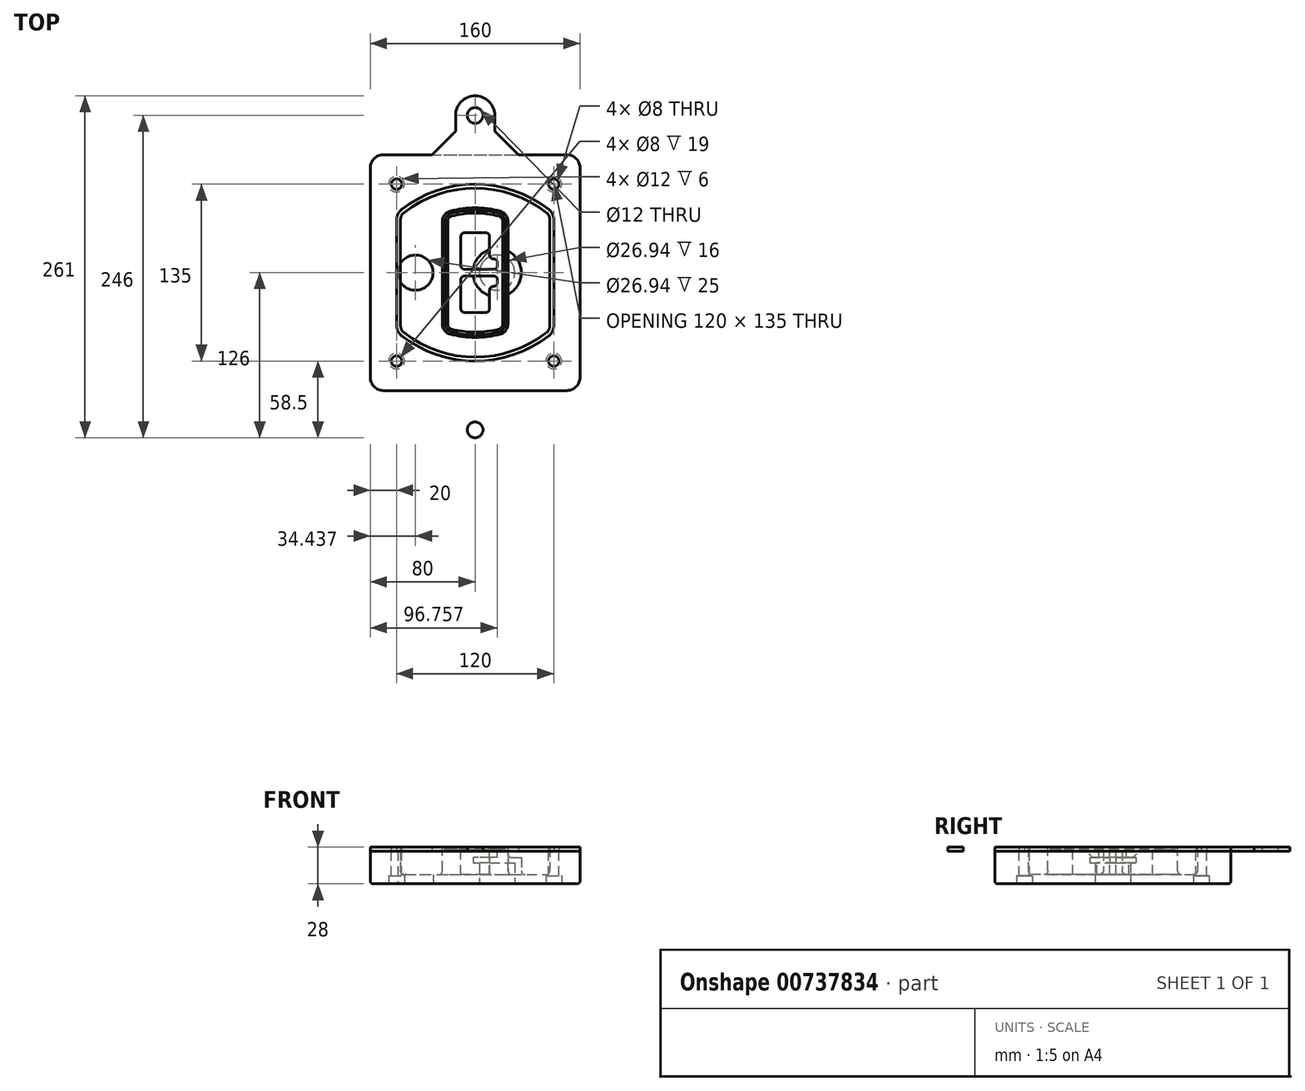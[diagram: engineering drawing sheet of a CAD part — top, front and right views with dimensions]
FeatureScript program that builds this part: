
annotation { "Feature Type Name" : "Feature", "Feature Type Description" : "" }
export const myFeature = defineFeature(function(context is Context, id is Id, definition is map)
    precondition{}
    {
        {
            var Q0;
            Q0=qCreatedBy(makeId("Top.planeOp"),FACE);
            var sketch = newSketch(context, id + "F0", { "sketchPlane" : qUnion([Q0])});
            skPoint(sketch, "E0.rect.middle", {"position": v(0, 0) * mm});
            skLineSegment(sketch, "E1.bottom", {"start": v(-70, -90) * mm, "end": v(70, -90) * mm});
            skLineSegment(sketch, "E1.top", {"start": v(-70, 90) * mm, "end": v(70, 90) * mm});
            skLineSegment(sketch, "E1.left", {"start": v(-80, -80) * mm, "end": v(-80, 80) * mm});
            skLineSegment(sketch, "E1.right", {"start": v(80, -80) * mm, "end": v(80, 80) * mm});
            skLineSegment(sketch, "E2", {"start": v(-80, 90) * mm, "end": v(80, -90) * mm, "construction": true});
            skLineSegment(sketch, "E3", {"start": v(80, 90) * mm, "end": v(-80, -90) * mm, "construction": true});
            skCircle(sketch, "E4", {"center": v(-60, 67.5) * mm, "radius": 4 * mm});
            skCircle(sketch, "E5", {"center": v(60, 67.5) * mm, "radius": 4 * mm});
            skCircle(sketch, "E6", {"center": v(60, -67.5) * mm, "radius": 4 * mm});
            skCircle(sketch, "E7", {"center": v(-60, -67.5) * mm, "radius": 4 * mm});
            skLineSegment(sketch, "E8", {"start": v(-60, 67.5) * mm, "end": v(60, 67.5) * mm, "construction": true});
            skLineSegment(sketch, "E9", {"start": v(60, 67.5) * mm, "end": v(60, -67.5) * mm, "construction": true});
            skLineSegment(sketch, "E10", {"start": v(60, -67.5) * mm, "end": v(-60, -67.5) * mm, "construction": true});
            skLineSegment(sketch, "E11", {"start": v(-60, -67.5) * mm, "end": v(-60, 67.5) * mm, "construction": true});
            skLineSegment(sketch, "E12", {"start": v(-60, 40.3) * mm, "end": v(-60, -40.3) * mm});
            skLineSegment(sketch, "E13", {"start": v(60, 40.3) * mm, "end": v(60, -40.3) * mm});
            skArc(sketch, "E14", {"start": v(56.15, 48.18) * mm, "mid": v(0, 67.5) * mm, "end": v(-56.15, 48.18) * mm});
            skArc(sketch, "E15", {"start": v(-56.15, -48.18) * mm, "mid": v(0, -67.5) * mm, "end": v(56.15, -48.18) * mm});
            skLineSegment(sketch, "E16", {"start": v(-60, 0) * mm, "end": v(60, 0) * mm, "construction": true});
            skPoint(sketch, "E17.visualSharp", {"position": v(-60, -45) * mm});
            skArc(sketch, "E17.filletArc", {"start": v(-60, -40.3) * mm, "mid": v(-58.99, -44.68) * mm, "end": v(-56.15, -48.18) * mm});
            skPoint(sketch, "E18.visualSharp", {"position": v(-60, 45) * mm});
            skArc(sketch, "E18.filletArc", {"start": v(-56.15, 48.18) * mm, "mid": v(-58.99, 44.68) * mm, "end": v(-60, 40.3) * mm});
            skPoint(sketch, "E19.visualSharp", {"position": v(60, 45) * mm});
            skArc(sketch, "E19.filletArc", {"start": v(60, 40.3) * mm, "mid": v(58.99, 44.68) * mm, "end": v(56.15, 48.18) * mm});
            skPoint(sketch, "E20.visualSharp", {"position": v(60, -45) * mm});
            skArc(sketch, "E20.filletArc", {"start": v(56.15, -48.18) * mm, "mid": v(58.99, -44.68) * mm, "end": v(60, -40.3) * mm});
            skPoint(sketch, "E21.visualSharp", {"position": v(-80, 90) * mm});
            skArc(sketch, "E21.filletArc", {"start": v(-70, 90) * mm, "mid": v(-77.07, 87.07) * mm, "end": v(-80, 80) * mm});
            skPoint(sketch, "E22.visualSharp", {"position": v(80, 90) * mm});
            skArc(sketch, "E22.filletArc", {"start": v(80, 80) * mm, "mid": v(77.07, 87.07) * mm, "end": v(70, 90) * mm});
            skPoint(sketch, "E23.visualSharp", {"position": v(80, -90) * mm});
            skArc(sketch, "E23.filletArc", {"start": v(70, -90) * mm, "mid": v(77.07, -87.07) * mm, "end": v(80, -80) * mm});
            skPoint(sketch, "E24.visualSharp", {"position": v(-80, -90) * mm});
            skArc(sketch, "E24.filletArc", {"start": v(-80, -80) * mm, "mid": v(-77.07, -87.07) * mm, "end": v(-70, -90) * mm});
            skArc(sketch, "E25.0", {"start": v(57, 40.3) * mm, "mid": v(56.3, 43.36) * mm, "end": v(54.3, 45.81) * mm});
            skLineSegment(sketch, "E25.1", {"start": v(57, 40.3) * mm, "end": v(57, -40.3) * mm});
            skArc(sketch, "E25.2", {"start": v(54.3, -45.81) * mm, "mid": v(56.3, -43.36) * mm, "end": v(57, -40.3) * mm});
            skArc(sketch, "E25.3", {"start": v(-54.3, -45.81) * mm, "mid": v(0, -64.5) * mm, "end": v(54.3, -45.81) * mm});
            skArc(sketch, "E25.4", {"start": v(-57, -40.3) * mm, "mid": v(-56.3, -43.36) * mm, "end": v(-54.3, -45.81) * mm});
            skArc(sketch, "E25.5", {"start": v(54.3, 45.81) * mm, "mid": v(0, 64.5) * mm, "end": v(-54.3, 45.81) * mm});
            skLineSegment(sketch, "E25.6", {"start": v(-57, 40.3) * mm, "end": v(-57, -40.3) * mm});
            skArc(sketch, "E25.7", {"start": v(-54.3, 45.81) * mm, "mid": v(-56.3, 43.36) * mm, "end": v(-57, 40.3) * mm});
            skArc(sketch, "E26.0", {"start": v(-58.62, 51.33) * mm, "mid": v(-62.58, 46.43) * mm, "end": v(-64, 40.3) * mm});
            skArc(sketch, "E26.1", {"start": v(58.62, 51.33) * mm, "mid": v(0, 71.5) * mm, "end": v(-58.62, 51.33) * mm});
            skArc(sketch, "E26.2", {"start": v(64, 40.3) * mm, "mid": v(62.58, 46.43) * mm, "end": v(58.62, 51.33) * mm});
            skLineSegment(sketch, "E26.3", {"start": v(64, 40.3) * mm, "end": v(64, -40.3) * mm});
            skArc(sketch, "E26.4", {"start": v(58.62, -51.33) * mm, "mid": v(62.58, -46.43) * mm, "end": v(64, -40.3) * mm});
            skLineSegment(sketch, "E26.5", {"start": v(-64, 40.3) * mm, "end": v(-64, -40.3) * mm});
            skArc(sketch, "E26.6", {"start": v(-58.62, -51.33) * mm, "mid": v(0, -71.5) * mm, "end": v(58.62, -51.33) * mm});
            skArc(sketch, "E26.7", {"start": v(-64, -40.3) * mm, "mid": v(-62.58, -46.43) * mm, "end": v(-58.62, -51.33) * mm});
            skSolve(sketch);
        }
        {
            var Q0;
            Q0=makeQuery(id+"F0.imprint","IMPRINT",FACE,{"disambiguationData":[TD([[makeQuery(id+"F0.imprint","IMPRINT",EDGE,{"derivedFrom":sQuery(id+"F0.wireOp",EDGE,"E1.bottom")}),1.0]])]});
            var Q1;
            Q1=makeQuery(id+"F0.imprint","IMPRINT",FACE,{"disambiguationData":[TD([[makeQuery(id+"F0.imprint","IMPRINT",EDGE,{"derivedFrom":sQuery(id+"F0.wireOp",EDGE,"E12")}),1.0]])]});
            var Q2;
            Q2=makeQuery(id+"F0.imprint","IMPRINT",FACE,{"disambiguationData":[TD([[makeQuery(id+"F0.imprint","IMPRINT",EDGE,{"derivedFrom":sQuery(id+"F0.wireOp",EDGE,"E25.0")}),1.0]])]});
            var Q3;
            Q3=makeQuery(id+"F0.imprint","IMPRINT",FACE,{"disambiguationData":[TD([[makeQuery(id+"F0.imprint","IMPRINT",EDGE,{"derivedFrom":sQuery(id+"F0.wireOp",EDGE,"E12")}),-1.0]])]});
            extrude(context, id + "F1", {"entities" : qUnion([Q0, Q1, Q2, Q3]), "oppositeDirection" : true, "depth" : 25 * mm});
        }
        {
            var Q0;
            Q0=makeQuery(id+"F0.imprint","IMPRINT",FACE,{"disambiguationData":[TD([[makeQuery(id+"F0.imprint","IMPRINT",EDGE,{"derivedFrom":sQuery(id+"F0.wireOp",EDGE,"E12")}),1.0]])]});
            extrude(context, id + "F2", {"entities" : qUnion([Q0]), "operationType" : NewBodyOperationType.ADD, "depth" : 3 * mm});
        }
        {
            var Q0;
            Q0=makeQuery(id+"F0.imprint","IMPRINT",FACE,{"disambiguationData":[TD([[makeQuery(id+"F0.imprint","IMPRINT",EDGE,{"derivedFrom":sQuery(id+"F0.wireOp",EDGE,"E25.0")}),1.0]])]});
            extrude(context, id + "F3", {"entities" : qUnion([Q0]), "operationType" : NewBodyOperationType.REMOVE, "oppositeDirection" : true, "depth" : 18 * mm});
        }
        {
            var Q0;
            Q0=makeQuery(id+"F2.opExtrude","CAP_FACE",FACE,{"disambiguationData":[OSD([sQuery(id+"F0.wireOp",EDGE,"E12"),sQuery(id+"F0.wireOp",EDGE,"E13"),sQuery(id+"F0.wireOp",EDGE,"E14"),sQuery(id+"F0.wireOp",EDGE,"E15"),sQuery(id+"F0.wireOp",EDGE,"E17.filletArc"),sQuery(id+"F0.wireOp",EDGE,"E18.filletArc"),sQuery(id+"F0.wireOp",EDGE,"E19.filletArc"),sQuery(id+"F0.wireOp",EDGE,"E20.filletArc"),sQuery(id+"F0.wireOp",EDGE,"E25.0"),sQuery(id+"F0.wireOp",EDGE,"E25.1"),sQuery(id+"F0.wireOp",EDGE,"E25.2"),sQuery(id+"F0.wireOp",EDGE,"E25.3"),sQuery(id+"F0.wireOp",EDGE,"E25.4"),sQuery(id+"F0.wireOp",EDGE,"E25.5"),sQuery(id+"F0.wireOp",EDGE,"E25.6"),sQuery(id+"F0.wireOp",EDGE,"E25.7")])],"isStart":false});
            var sketch = newSketch(context, id + "F4", { "sketchPlane" : qUnion([Q0])});
            skArc(sketch, "E27.0", {"start": v(-19.08, -46.97) * mm, "mid": v(0, -49.5) * mm, "end": v(19.08, -46.97) * mm});
            skArc(sketch, "E28.0", {"start": v(19.08, 46.97) * mm, "mid": v(0, 49.5) * mm, "end": v(-19.08, 46.97) * mm});
            skLineSegment(sketch, "E29", {"start": v(-25, 39.25) * mm, "end": v(-25, -39.25) * mm});
            skLineSegment(sketch, "E30", {"start": v(25, 39.25) * mm, "end": v(25, -39.25) * mm});
            skLineSegment(sketch, "E31", {"start": v(-25, 45.1) * mm, "end": v(25, 45.1) * mm, "construction": true});
            skLineSegment(sketch, "E32", {"start": v(-25, -45.1) * mm, "end": v(25, -45.1) * mm, "construction": true});
            skPoint(sketch, "E33.visualSharp", {"position": v(-25, 45.1) * mm});
            skArc(sketch, "E33.filletArc", {"start": v(-19.08, 46.97) * mm, "mid": v(-23.35, 44.11) * mm, "end": v(-25, 39.25) * mm});
            skPoint(sketch, "E34.visualSharp", {"position": v(25, 45.1) * mm});
            skArc(sketch, "E34.filletArc", {"start": v(25, 39.25) * mm, "mid": v(23.35, 44.11) * mm, "end": v(19.08, 46.97) * mm});
            skPoint(sketch, "E35.visualSharp", {"position": v(25, -45.1) * mm});
            skArc(sketch, "E35.filletArc", {"start": v(19.08, -46.97) * mm, "mid": v(23.35, -44.11) * mm, "end": v(25, -39.25) * mm});
            skPoint(sketch, "E36.visualSharp", {"position": v(-25, -45.1) * mm});
            skArc(sketch, "E36.filletArc", {"start": v(-25, -39.25) * mm, "mid": v(-23.35, -44.11) * mm, "end": v(-19.08, -46.97) * mm});
            skArc(sketch, "E37.0", {"start": v(54.3, 45.81) * mm, "mid": v(0, 64.5) * mm, "end": v(-54.3, 45.81) * mm});
            skArc(sketch, "E37.1", {"start": v(-54.3, 45.81) * mm, "mid": v(-56.3, 43.36) * mm, "end": v(-57, 40.3) * mm});
            skLineSegment(sketch, "E37.2", {"start": v(-57, 40.3) * mm, "end": v(-57, -40.3) * mm});
            skArc(sketch, "E37.3", {"start": v(-57, -40.3) * mm, "mid": v(-56.3, -43.36) * mm, "end": v(-54.3, -45.81) * mm});
            skArc(sketch, "E37.4", {"start": v(-54.3, -45.81) * mm, "mid": v(0, -64.5) * mm, "end": v(54.3, -45.81) * mm});
            skArc(sketch, "E37.5", {"start": v(54.3, -45.81) * mm, "mid": v(56.3, -43.36) * mm, "end": v(57, -40.3) * mm});
            skLineSegment(sketch, "E37.6", {"start": v(57, 40.3) * mm, "end": v(57, -40.3) * mm});
            skArc(sketch, "E37.7", {"start": v(57, 40.3) * mm, "mid": v(56.3, 43.36) * mm, "end": v(54.3, 45.81) * mm});
            skLineSegment(sketch, "E38.0", {"start": v(23, 39.25) * mm, "end": v(23, -39.25) * mm});
            skArc(sketch, "E38.1", {"start": v(18.56, -45.04) * mm, "mid": v(21.76, -42.9) * mm, "end": v(23, -39.25) * mm});
            skArc(sketch, "E38.2", {"start": v(-18.56, -45.04) * mm, "mid": v(0, -47.5) * mm, "end": v(18.56, -45.04) * mm});
            skArc(sketch, "E38.3", {"start": v(-23, -39.25) * mm, "mid": v(-21.76, -42.9) * mm, "end": v(-18.56, -45.04) * mm});
            skLineSegment(sketch, "E38.4", {"start": v(-23, 39.25) * mm, "end": v(-23, -39.25) * mm});
            skArc(sketch, "E38.5", {"start": v(23, 39.25) * mm, "mid": v(21.76, 42.9) * mm, "end": v(18.56, 45.04) * mm});
            skArc(sketch, "E38.6", {"start": v(-18.56, 45.04) * mm, "mid": v(-21.76, 42.9) * mm, "end": v(-23, 39.25) * mm});
            skArc(sketch, "E38.7", {"start": v(18.56, 45.04) * mm, "mid": v(0, 47.5) * mm, "end": v(-18.56, 45.04) * mm});
            skArc(sketch, "E39.0", {"start": v(21, 39.25) * mm, "mid": v(20.18, 41.68) * mm, "end": v(18.04, 43.1) * mm});
            skLineSegment(sketch, "E39.1", {"start": v(21, 39.25) * mm, "end": v(21, -39.25) * mm});
            skArc(sketch, "E39.2", {"start": v(18.04, -43.1) * mm, "mid": v(20.18, -41.68) * mm, "end": v(21, -39.25) * mm});
            skArc(sketch, "E39.3", {"start": v(-18.04, -43.1) * mm, "mid": v(0, -45.5) * mm, "end": v(18.04, -43.1) * mm});
            skArc(sketch, "E39.4", {"start": v(-21, -39.25) * mm, "mid": v(-20.18, -41.68) * mm, "end": v(-18.04, -43.1) * mm});
            skArc(sketch, "E39.5", {"start": v(18.04, 43.1) * mm, "mid": v(0, 45.5) * mm, "end": v(-18.04, 43.1) * mm});
            skLineSegment(sketch, "E39.6", {"start": v(-21, 39.25) * mm, "end": v(-21, -39.25) * mm});
            skArc(sketch, "E39.7", {"start": v(-18.04, 43.1) * mm, "mid": v(-20.18, 41.68) * mm, "end": v(-21, 39.25) * mm});
            skLineSegment(sketch, "E40", {"start": v(-25, 0) * mm, "end": v(25, 0) * mm, "construction": true});
            skLineSegment(sketch, "E41", {"start": v(-11, 5.5) * mm, "end": v(-11, 27.5) * mm});
            skLineSegment(sketch, "E42", {"start": v(-8, 30.5) * mm, "end": v(8, 30.5) * mm});
            skLineSegment(sketch, "E43", {"start": v(11, 27.5) * mm, "end": v(11, 13.5) * mm});
            skLineSegment(sketch, "E44", {"start": v(14, 10.5) * mm, "end": v(14, 10.5) * mm});
            skLineSegment(sketch, "E45", {"start": v(17, 7.5) * mm, "end": v(17, 5.5) * mm});
            skLineSegment(sketch, "E46", {"start": v(14, 2.5) * mm, "end": v(-8, 2.5) * mm});
            skPoint(sketch, "E47.visualSharp", {"position": v(-11, 30.5) * mm});
            skArc(sketch, "E47.filletArc", {"start": v(-8, 30.5) * mm, "mid": v(-10.12, 29.62) * mm, "end": v(-11, 27.5) * mm});
            skPoint(sketch, "E48.visualSharp", {"position": v(11, 30.5) * mm});
            skArc(sketch, "E48.filletArc", {"start": v(11, 27.5) * mm, "mid": v(10.12, 29.62) * mm, "end": v(8, 30.5) * mm});
            skPoint(sketch, "E49.visualSharp", {"position": v(11, 10.5) * mm});
            skArc(sketch, "E49.filletArc", {"start": v(11, 13.5) * mm, "mid": v(11.88, 11.38) * mm, "end": v(14, 10.5) * mm});
            skPoint(sketch, "E50.visualSharp", {"position": v(17, 10.5) * mm});
            skArc(sketch, "E50.filletArc", {"start": v(17, 7.5) * mm, "mid": v(16.12, 9.62) * mm, "end": v(14, 10.5) * mm});
            skPoint(sketch, "E51.visualSharp", {"position": v(17, 2.5) * mm});
            skArc(sketch, "E51.filletArc", {"start": v(14, 2.5) * mm, "mid": v(16.12, 3.38) * mm, "end": v(17, 5.5) * mm});
            skPoint(sketch, "E52.visualSharp", {"position": v(-11, 2.5) * mm});
            skArc(sketch, "E52.filletArc", {"start": v(-11, 5.5) * mm, "mid": v(-10.12, 3.38) * mm, "end": v(-8, 2.5) * mm});
            skLineSegment(sketch, "E53.0.MirrorCS", {"start": v(14, -2.5) * mm, "end": v(-8, -2.5) * mm});
            skArc(sketch, "E54.0.MirrorCS", {"start": v(-11, -5.5) * mm, "mid": v(-10.12, -3.38) * mm, "end": v(-8, -2.5) * mm});
            skLineSegment(sketch, "E55.0.MirrorCS", {"start": v(-11, -5.5) * mm, "end": v(-11, -27.5) * mm});
            skArc(sketch, "E56.0.MirrorCS", {"start": v(-8, -30.5) * mm, "mid": v(-10.12, -29.62) * mm, "end": v(-11, -27.5) * mm});
            skLineSegment(sketch, "E57.0.MirrorCS", {"start": v(-8, -30.5) * mm, "end": v(8, -30.5) * mm});
            skArc(sketch, "E58.0.MirrorCS", {"start": v(11, -27.5) * mm, "mid": v(10.12, -29.62) * mm, "end": v(8, -30.5) * mm});
            skLineSegment(sketch, "E59.0.MirrorCS", {"start": v(11, -27.5) * mm, "end": v(11, -13.5) * mm});
            skArc(sketch, "E60.0.MirrorCS", {"start": v(11, -13.5) * mm, "mid": v(11.88, -11.38) * mm, "end": v(14, -10.5) * mm});
            skArc(sketch, "E61.0.MirrorCS", {"start": v(17, -7.5) * mm, "mid": v(16.12, -9.62) * mm, "end": v(14, -10.5) * mm});
            skLineSegment(sketch, "E62.0.MirrorCS", {"start": v(17, -7.5) * mm, "end": v(17, -5.5) * mm});
            skArc(sketch, "E63.0.MirrorCS", {"start": v(14, -2.5) * mm, "mid": v(16.12, -3.38) * mm, "end": v(17, -5.5) * mm});
            skSolve(sketch);
        }
        {
            var Q0;
            Q0=makeQuery(id+"F4.imprint","IMPRINT",FACE,{"disambiguationData":[TD([[makeQuery(id+"F4.imprint","IMPRINT",EDGE,{"derivedFrom":sQuery(id+"F4.wireOp",EDGE,"E27.0")}),1.0]])]});
            var Q1;
            Q1=makeQuery(id+"F4.imprint","IMPRINT",FACE,{"disambiguationData":[TD([[makeQuery(id+"F4.imprint","IMPRINT",EDGE,{"derivedFrom":sQuery(id+"F4.wireOp",EDGE,"E38.0")}),-1.0]])]});
            var Q2;
            Q2=makeQuery(id+"F4.imprint","IMPRINT",FACE,{"disambiguationData":[TD([[makeQuery(id+"F4.imprint","IMPRINT",EDGE,{"derivedFrom":sQuery(id+"F4.wireOp",EDGE,"E39.0")}),1.0]])]});
            extrude(context, id + "F5", {"entities" : qUnion([Q0, Q1, Q2]), "operationType" : NewBodyOperationType.ADD, "endBound" : BoundingType.UP_TO_NEXT, "oppositeDirection" : true, "depth" : 25 * mm});
        }
        {
            var Q0;
            Q0=makeQuery(id+"F4.imprint","IMPRINT",FACE,{"disambiguationData":[TD([[makeQuery(id+"F4.imprint","IMPRINT",EDGE,{"derivedFrom":sQuery(id+"F4.wireOp",EDGE,"E38.0")}),-1.0]])]});
            extrude(context, id + "F6", {"entities" : qUnion([Q0]), "operationType" : NewBodyOperationType.REMOVE, "oppositeDirection" : true, "depth" : 2 * mm});
        }
        {
            var Q0;
            Q0=makeQuery(id+"F1.opExtrude","CAP_FACE",FACE,{"disambiguationData":[OSD([sQuery(id+"F0.wireOp",EDGE,"E1.bottom"),sQuery(id+"F0.wireOp",EDGE,"E1.top"),sQuery(id+"F0.wireOp",EDGE,"E1.left"),sQuery(id+"F0.wireOp",EDGE,"E1.right"),sQuery(id+"F0.wireOp",EDGE,"E4"),sQuery(id+"F0.wireOp",EDGE,"E5"),sQuery(id+"F0.wireOp",EDGE,"E6"),sQuery(id+"F0.wireOp",EDGE,"E7"),sQuery(id+"F0.wireOp",EDGE,"E21.filletArc"),sQuery(id+"F0.wireOp",EDGE,"E22.filletArc"),sQuery(id+"F0.wireOp",EDGE,"E23.filletArc"),sQuery(id+"F0.wireOp",EDGE,"E24.filletArc")])],"isStart":false});
            var sketch = newSketch(context, id + "F7", { "sketchPlane" : qUnion([Q0])});
            skCircle(sketch, "E64", {"center": v(16.76, 0) * mm, "radius": 13.47 * mm});
            skCircle(sketch, "E65", {"center": v(-45.56, 0) * mm, "radius": 13.47 * mm});
            skLineSegment(sketch, "E66", {"start": v(80, 0) * mm, "end": v(-80, 0) * mm});
            skCircle(sketch, "E67", {"center": v(16.76, 0) * mm, "radius": 18.47 * mm});
            skCircle(sketch, "E68", {"center": v(60, -67.5) * mm, "radius": 6 * mm});
            skCircle(sketch, "E69", {"center": v(-60, -67.5) * mm, "radius": 6 * mm});
            skCircle(sketch, "E70", {"center": v(-60, 67.5) * mm, "radius": 6 * mm});
            skCircle(sketch, "E71", {"center": v(60, 67.5) * mm, "radius": 6 * mm});
            skSolve(sketch);
        }
        {
            var Q0;
            {var subQ1=sQuery(id+"F7.wireOp",EDGE,"E66");var subQ4=sQuery(id+"F7.wireOp",EDGE,"E64");var subQ6=makeQuery(id+"F7.imprint","INTERSECT",VERTEX,{"disambiguationData":[OD(0.0)],"derivedFrom":[subQ4,subQ1]});Q0=makeQuery(id+"F7.imprint","IMPRINT",FACE,{"disambiguationData":[TD([[makeQuery(id+"F7.imprint","IMPRINT",EDGE,{"disambiguationData":[TD([[subQ6,-1.0]])],"derivedFrom":subQ4}),-1.0]])]});}
            var Q1;
            {var subQ0=sQuery(id+"F7.wireOp",EDGE,"E66");var subQ1=sQuery(id+"F7.wireOp",EDGE,"E64");var subQ3=makeQuery(id+"F7.imprint","INTERSECT",VERTEX,{"disambiguationData":[OD(0.0)],"derivedFrom":[subQ1,subQ0]});Q1=makeQuery(id+"F7.imprint","IMPRINT",FACE,{"disambiguationData":[TD([[makeQuery(id+"F7.imprint","IMPRINT",EDGE,{"disambiguationData":[TD([[subQ3,-1.0]])],"derivedFrom":subQ1}),1.0]])]});}
            var Q2;
            {var subQ0=sQuery(id+"F7.wireOp",EDGE,"E66");var subQ1=sQuery(id+"F7.wireOp",EDGE,"E64");var subQ3=makeQuery(id+"F7.imprint","INTERSECT",VERTEX,{"disambiguationData":[OD(0.0)],"derivedFrom":[subQ1,subQ0]});Q2=makeQuery(id+"F7.imprint","IMPRINT",FACE,{"disambiguationData":[TD([[makeQuery(id+"F7.imprint","IMPRINT",EDGE,{"disambiguationData":[TD([[subQ3,1.0]])],"derivedFrom":subQ1}),1.0]])]});}
            var Q3;
            {var subQ1=sQuery(id+"F7.wireOp",EDGE,"E66");var subQ4=sQuery(id+"F7.wireOp",EDGE,"E64");var subQ6=makeQuery(id+"F7.imprint","INTERSECT",VERTEX,{"disambiguationData":[OD(0.0)],"derivedFrom":[subQ4,subQ1]});Q3=makeQuery(id+"F7.imprint","IMPRINT",FACE,{"disambiguationData":[TD([[makeQuery(id+"F7.imprint","IMPRINT",EDGE,{"disambiguationData":[TD([[subQ6,1.0]])],"derivedFrom":subQ4}),-1.0]])]});}
            extrude(context, id + "F8", {"entities" : qUnion([Q0, Q1, Q2, Q3]), "operationType" : NewBodyOperationType.ADD, "oppositeDirection" : true, "depth" : 20 * mm});
        }
        {
            var Q0;
            {var subQ0=sQuery(id+"F7.wireOp",EDGE,"E66");var subQ1=sQuery(id+"F7.wireOp",EDGE,"E64");var subQ3=makeQuery(id+"F7.imprint","INTERSECT",VERTEX,{"disambiguationData":[OD(0.0)],"derivedFrom":[subQ1,subQ0]});Q0=makeQuery(id+"F7.imprint","IMPRINT",FACE,{"disambiguationData":[TD([[makeQuery(id+"F7.imprint","IMPRINT",EDGE,{"disambiguationData":[TD([[subQ3,-1.0]])],"derivedFrom":subQ1}),1.0]])]});}
            var Q1;
            {var subQ0=sQuery(id+"F7.wireOp",EDGE,"E66");var subQ1=sQuery(id+"F7.wireOp",EDGE,"E64");var subQ3=makeQuery(id+"F7.imprint","INTERSECT",VERTEX,{"disambiguationData":[OD(0.0)],"derivedFrom":[subQ1,subQ0]});Q1=makeQuery(id+"F7.imprint","IMPRINT",FACE,{"disambiguationData":[TD([[makeQuery(id+"F7.imprint","IMPRINT",EDGE,{"disambiguationData":[TD([[subQ3,1.0]])],"derivedFrom":subQ1}),1.0]])]});}
            extrude(context, id + "F9", {"entities" : qUnion([Q0, Q1]), "operationType" : NewBodyOperationType.REMOVE, "oppositeDirection" : true, "depth" : 16 * mm});
        }
        {
            var Q0;
            {var subQ0=sQuery(id+"F7.wireOp",EDGE,"E66");var subQ1=sQuery(id+"F7.wireOp",EDGE,"E65");var subQ3=makeQuery(id+"F7.imprint","INTERSECT",VERTEX,{"disambiguationData":[OD(0.0)],"derivedFrom":[subQ1,subQ0]});Q0=makeQuery(id+"F7.imprint","IMPRINT",FACE,{"disambiguationData":[TD([[makeQuery(id+"F7.imprint","IMPRINT",EDGE,{"disambiguationData":[TD([[subQ3,-1.0]])],"derivedFrom":subQ1}),1.0]])]});}
            var Q1;
            {var subQ0=sQuery(id+"F7.wireOp",EDGE,"E66");var subQ1=sQuery(id+"F7.wireOp",EDGE,"E65");var subQ3=makeQuery(id+"F7.imprint","INTERSECT",VERTEX,{"disambiguationData":[OD(0.0)],"derivedFrom":[subQ1,subQ0]});Q1=makeQuery(id+"F7.imprint","IMPRINT",FACE,{"disambiguationData":[TD([[makeQuery(id+"F7.imprint","IMPRINT",EDGE,{"disambiguationData":[TD([[subQ3,1.0]])],"derivedFrom":subQ1}),1.0]])]});}
            extrude(context, id + "F10", {"entities" : qUnion([Q0, Q1]), "operationType" : NewBodyOperationType.REMOVE, "oppositeDirection" : true, "depth" : 25 * mm});
        }
        {
            var Q0;
            Q0=makeQuery(id+"F7.imprint","IMPRINT",FACE,{"disambiguationData":[TD([[makeQuery(id+"F7.imprint","IMPRINT",EDGE,{"derivedFrom":sQuery(id+"F7.wireOp",EDGE,"E68")}),1.0]])]});
            var Q1;
            Q1=makeQuery(id+"F7.imprint","IMPRINT",FACE,{"disambiguationData":[TD([[makeQuery(id+"F7.imprint","IMPRINT",EDGE,{"derivedFrom":makeQuery(id+"F1.opExtrude","CAP_EDGE",EDGE,{"disambiguationData":[OSD([sQuery(id+"F0.wireOp",EDGE,"E5")])],"isStart":false})}),-1.0]])]});
            var Q2;
            Q2=makeQuery(id+"F7.imprint","IMPRINT",FACE,{"disambiguationData":[TD([[makeQuery(id+"F7.imprint","IMPRINT",EDGE,{"derivedFrom":sQuery(id+"F7.wireOp",EDGE,"E69")}),1.0]])]});
            var Q3;
            Q3=makeQuery(id+"F7.imprint","IMPRINT",FACE,{"disambiguationData":[TD([[makeQuery(id+"F7.imprint","IMPRINT",EDGE,{"derivedFrom":makeQuery(id+"F1.opExtrude","CAP_EDGE",EDGE,{"disambiguationData":[OSD([sQuery(id+"F0.wireOp",EDGE,"E4")])],"isStart":false})}),-1.0]])]});
            var Q4;
            Q4=makeQuery(id+"F7.imprint","IMPRINT",FACE,{"disambiguationData":[TD([[makeQuery(id+"F7.imprint","IMPRINT",EDGE,{"derivedFrom":sQuery(id+"F7.wireOp",EDGE,"E70")}),1.0]])]});
            var Q5;
            Q5=makeQuery(id+"F7.imprint","IMPRINT",FACE,{"disambiguationData":[TD([[makeQuery(id+"F7.imprint","IMPRINT",EDGE,{"derivedFrom":makeQuery(id+"F1.opExtrude","CAP_EDGE",EDGE,{"disambiguationData":[OSD([sQuery(id+"F0.wireOp",EDGE,"E7")])],"isStart":false})}),-1.0]])]});
            var Q6;
            Q6=makeQuery(id+"F7.imprint","IMPRINT",FACE,{"disambiguationData":[TD([[makeQuery(id+"F7.imprint","IMPRINT",EDGE,{"derivedFrom":sQuery(id+"F7.wireOp",EDGE,"E71")}),1.0]])]});
            var Q7;
            Q7=makeQuery(id+"F7.imprint","IMPRINT",FACE,{"disambiguationData":[TD([[makeQuery(id+"F7.imprint","IMPRINT",EDGE,{"derivedFrom":makeQuery(id+"F1.opExtrude","CAP_EDGE",EDGE,{"disambiguationData":[OSD([sQuery(id+"F0.wireOp",EDGE,"E6")])],"isStart":false})}),-1.0]])]});
            extrude(context, id + "F11", {"entities" : qUnion([Q0, Q1, Q2, Q3, Q4, Q5, Q6, Q7]), "operationType" : NewBodyOperationType.REMOVE, "oppositeDirection" : true, "depth" : 6 * mm});
        }
        {
            var Q0;
            Q0=makeQuery(id+"F9.boolean.opBoolean","COPY",FACE,{"derivedFrom":makeQuery(id+"F9.opExtrude","CAP_FACE",FACE,{"disambiguationData":[OSD([sQuery(id+"F7.wireOp",EDGE,"E64")])],"isStart":false})});
            var sketch = newSketch(context, id + "F12", { "sketchPlane" : qUnion([Q0])});
            skArc(sketch, "E72.0", {"start": v(11, 17.55) * mm, "mid": v(2.57, 11.82) * mm, "end": v(-1.54, 2.5) * mm});
            skArc(sketch, "E72.1", {"start": v(-1.54, -2.5) * mm, "mid": v(2.57, -11.82) * mm, "end": v(11, -17.55) * mm});
            skLineSegment(sketch, "E73", {"start": v(-1.54, -2.5) * mm, "end": v(14, -2.5) * mm});
            skLineSegment(sketch, "E74.0", {"start": v(14, 2.5) * mm, "end": v(-1.54, 2.5) * mm});
            skArc(sketch, "E74.1", {"start": v(14, 2.5) * mm, "mid": v(16.12, 3.38) * mm, "end": v(17, 5.5) * mm});
            skLineSegment(sketch, "E74.2", {"start": v(17, 7.5) * mm, "end": v(17, 5.5) * mm});
            skArc(sketch, "E74.3", {"start": v(17, 7.5) * mm, "mid": v(16.12, 9.62) * mm, "end": v(14, 10.5) * mm});
            skArc(sketch, "E74.4", {"start": v(11, 13.5) * mm, "mid": v(11.88, 11.38) * mm, "end": v(14, 10.5) * mm});
            skLineSegment(sketch, "E74.5", {"start": v(11, 17.55) * mm, "end": v(11, 13.5) * mm});
            skLineSegment(sketch, "E74.7", {"start": v(14, -2.5) * mm, "end": v(-1.54, -2.5) * mm});
            skArc(sketch, "E74.8", {"start": v(14, -2.5) * mm, "mid": v(16.12, -3.38) * mm, "end": v(17, -5.5) * mm});
            skLineSegment(sketch, "E74.9", {"start": v(17, -7.5) * mm, "end": v(17, -5.5) * mm});
            skArc(sketch, "E74.10", {"start": v(17, -7.5) * mm, "mid": v(16.12, -9.62) * mm, "end": v(14, -10.5) * mm});
            skArc(sketch, "E74.11", {"start": v(11, -13.5) * mm, "mid": v(11.88, -11.38) * mm, "end": v(14, -10.5) * mm});
            skLineSegment(sketch, "E74.12", {"start": v(11, -17.55) * mm, "end": v(11, -13.5) * mm});
            skPoint(sketch, "E75.orphan", {"position": v(11, -27.5) * mm});
            skPoint(sketch, "E76.orphan", {"position": v(-8, -2.5) * mm});
            skPoint(sketch, "E77.orphan", {"position": v(-8, 2.5) * mm});
            skPoint(sketch, "E78.orphan", {"position": v(11, 27.5) * mm});
            skSolve(sketch);
        }
        {
            var Q0;
            {var subQ7=sQuery(id+"F12.wireOp",EDGE,"E72.0");var subQ14=sQuery(id+"F12.wireOp",EDGE,"E72.1");var subQ16=sQuery(id+"F12.wireOp",EDGE,"E74.1");var subQ18=sQuery(id+"F12.wireOp",EDGE,"E74.8");Q0=qUnion([makeQuery(id+"F12.imprint","IMPRINT",FACE,{"disambiguationData":[TD([[makeQuery(id+"F12.imprint","IMPRINT",EDGE,{"derivedFrom":subQ7}),1.0]])]}),makeQuery(id+"F12.imprint","IMPRINT",FACE,{"disambiguationData":[TD([[makeQuery(id+"F12.imprint","IMPRINT",EDGE,{"derivedFrom":subQ14}),1.0]])]}),makeQuery(id+"F12.imprint","IMPRINT",FACE,{"disambiguationData":[TD([[makeQuery(id+"F12.imprint","IMPRINT",EDGE,{"derivedFrom":subQ16}),1.0]])]}),makeQuery(id+"F12.imprint","IMPRINT",FACE,{"disambiguationData":[TD([[makeQuery(id+"F12.imprint","IMPRINT",EDGE,{"derivedFrom":subQ18}),-1.0]])]})]);}
            var Q1;
            Q1=makeQuery(id+"F5.boolean.opBoolean","SPLIT",FACE,{"disambiguationData":[TD([makeQuery(id+"F5.opExtrude","SWEPT_FACE",FACE,{"disambiguationData":[OSD([sQuery(id+"F4.wireOp",EDGE,"E41")])]})])],"derivedFrom":makeQuery(id+"F3.boolean.opBoolean","COPY",FACE,{"derivedFrom":makeQuery(id+"F3.opExtrude","CAP_FACE",FACE,{"disambiguationData":[OSD([sQuery(id+"F0.wireOp",EDGE,"E25.0"),sQuery(id+"F0.wireOp",EDGE,"E25.1"),sQuery(id+"F0.wireOp",EDGE,"E25.2"),sQuery(id+"F0.wireOp",EDGE,"E25.3"),sQuery(id+"F0.wireOp",EDGE,"E25.4"),sQuery(id+"F0.wireOp",EDGE,"E25.5"),sQuery(id+"F0.wireOp",EDGE,"E25.6"),sQuery(id+"F0.wireOp",EDGE,"E25.7")])],"isStart":false})})});
            extrude(context, id + "F13", {"entities" : qUnion([Q0]), "operationType" : NewBodyOperationType.REMOVE, "endBound" : BoundingType.UP_TO_SURFACE, "endBoundEntityFace" : qUnion([Q1]), "depth" : 25 * mm});
        }
        {
            var Q0;
            Q0=makeQuery(id+"F3.boolean.opBoolean","COPY",EDGE,{"derivedFrom":makeQuery(id+"F3.opExtrude","CAP_EDGE",EDGE,{"disambiguationData":[OSD([sQuery(id+"F0.wireOp",EDGE,"E25.6")])],"isStart":false})});
            var Q1;
            Q1=makeQuery(id+"F8.boolean.opBoolean","INTERSECT",EDGE,{"derivedFrom":[makeQuery(id+"F5.opExtrude","SWEPT_FACE",FACE,{"disambiguationData":[OSD([sQuery(id+"F4.wireOp",EDGE,"E30")])]}),makeQuery(id+"F8.opExtrude","CAP_FACE",FACE,{"disambiguationData":[OSD([sQuery(id+"F7.wireOp",EDGE,"E67")])],"isStart":false})]});
            var Q2;
            Q2=makeQuery(id+"F8.boolean.opBoolean","INTERSECT",EDGE,{"disambiguationData":[OD(1.0)],"derivedFrom":[makeQuery(id+"F5.opExtrude","SWEPT_FACE",FACE,{"disambiguationData":[OSD([sQuery(id+"F4.wireOp",EDGE,"E30")])]}),makeQuery(id+"F8.opExtrude","SWEPT_FACE",FACE,{"disambiguationData":[OSD([sQuery(id+"F7.wireOp",EDGE,"E67")])]})]});
            var Q3;
            {var subQ0=sQuery(id+"F4.wireOp",EDGE,"E30");Q3=makeQuery(id+"F8.boolean.opBoolean","SPLIT",EDGE,{"disambiguationData":[TD([makeQuery(id+"F5.opExtrude","SWEPT_FACE",FACE,{"disambiguationData":[OSD([sQuery(id+"F4.wireOp",EDGE,"E35.filletArc")])]})])],"derivedFrom":makeQuery(id+"F5.opExtrude","CAP_EDGE",EDGE,{"disambiguationData":[OSD([subQ0])],"isStart":false})});}
            var Q4;
            {var subQ0=sQuery(id+"F0.wireOp",EDGE,"E25.7");var subQ1=sQuery(id+"F0.wireOp",EDGE,"E25.1");var subQ2=sQuery(id+"F0.wireOp",EDGE,"E25.6");var subQ3=sQuery(id+"F0.wireOp",EDGE,"E25.5");var subQ4=sQuery(id+"F0.wireOp",EDGE,"E25.4");var subQ5=sQuery(id+"F0.wireOp",EDGE,"E25.0");var subQ6=sQuery(id+"F0.wireOp",EDGE,"E25.2");var subQ7=sQuery(id+"F0.wireOp",EDGE,"E25.3");Q4=makeQuery(id+"F8.boolean.opBoolean","INTERSECT",EDGE,{"derivedFrom":[makeQuery(id+"F5.boolean.opBoolean","SPLIT",FACE,{"disambiguationData":[TD([makeQuery(id+"F2.opExtrude","SWEPT_FACE",FACE,{"disambiguationData":[OSD([subQ5])]})])],"derivedFrom":makeQuery(id+"F3.boolean.opBoolean","COPY",FACE,{"derivedFrom":makeQuery(id+"F3.opExtrude","CAP_FACE",FACE,{"disambiguationData":[OSD([subQ5,subQ1,subQ6,subQ7,subQ4,subQ3,subQ2,subQ0])],"isStart":false})})}),makeQuery(id+"F8.opExtrude","SWEPT_FACE",FACE,{"disambiguationData":[OSD([sQuery(id+"F7.wireOp",EDGE,"E67")])]})]});}
            var Q5;
            Q5=makeQuery(id+"F8.boolean.opBoolean","INTERSECT",EDGE,{"disambiguationData":[OD(0.0)],"derivedFrom":[makeQuery(id+"F5.opExtrude","SWEPT_FACE",FACE,{"disambiguationData":[OSD([sQuery(id+"F4.wireOp",EDGE,"E30")])]}),makeQuery(id+"F8.opExtrude","SWEPT_FACE",FACE,{"disambiguationData":[OSD([sQuery(id+"F7.wireOp",EDGE,"E67")])]})]});
            fillet(context, id + "F14", {"entities" : qUnion([Q0, Q1, Q2, Q3, Q4, Q5]), "radius" : 3 * mm, "tangentPropagation" : true, "allowEdgeOverflow" : false});
        }
        {
            var Q0;
            Q0=makeQuery(id+"F1.opExtrude","CAP_EDGE",EDGE,{"disambiguationData":[OSD([sQuery(id+"F0.wireOp",EDGE,"E1.bottom")])],"isStart":false});
            fillet(context, id + "F15", {"entities" : qUnion([Q0]), "radius" : 2 * mm, "tangentPropagation" : true, "allowEdgeOverflow" : false});
        }
        {
            var Q0;
            {var subQ0=sQuery(id+"F0.wireOp",EDGE,"E21.filletArc");var subQ1=sQuery(id+"F0.wireOp",EDGE,"E7");var subQ2=sQuery(id+"F0.wireOp",EDGE,"E6");var subQ3=sQuery(id+"F0.wireOp",EDGE,"E5");var subQ4=sQuery(id+"F0.wireOp",EDGE,"E4");var subQ5=sQuery(id+"F0.wireOp",EDGE,"E22.filletArc");var subQ6=sQuery(id+"F0.wireOp",EDGE,"E1.bottom");var subQ7=sQuery(id+"F0.wireOp",EDGE,"E1.right");var subQ8=sQuery(id+"F0.wireOp",EDGE,"E1.top");var subQ9=sQuery(id+"F0.wireOp",EDGE,"E1.left");var subQ10=sQuery(id+"F0.wireOp",EDGE,"E23.filletArc");var subQ11=sQuery(id+"F0.wireOp",EDGE,"E24.filletArc");Q0=makeQuery(id+"F2.boolean.opBoolean","SPLIT",FACE,{"disambiguationData":[TD([makeQuery(id+"F1.opExtrude","SWEPT_FACE",FACE,{"disambiguationData":[OSD([subQ6])]})])],"derivedFrom":makeQuery(id+"F1.opExtrude","CAP_FACE",FACE,{"disambiguationData":[OSD([subQ6,subQ8,subQ9,subQ7,subQ4,subQ3,subQ2,subQ1,subQ0,subQ5,subQ10,subQ11])],"isStart":true})});}
            var sketch = newSketch(context, id + "F16", { "sketchPlane" : qUnion([Q0])});
            skLineSegment(sketch, "E79", {"start": v(0, 90) * mm, "end": v(0, 120) * mm, "construction": true});
            skCircle(sketch, "E80", {"center": v(0, 120) * mm, "radius": 6 * mm});
            skLineSegment(sketch, "E81", {"start": v(-33, 90) * mm, "end": v(-15, 108) * mm});
            skLineSegment(sketch, "E82", {"start": v(-15, 108) * mm, "end": v(-15, 120) * mm});
            skLineSegment(sketch, "E83", {"start": v(33, 90) * mm, "end": v(15, 108) * mm});
            skLineSegment(sketch, "E84", {"start": v(15, 108) * mm, "end": v(15, 120) * mm});
            skArc(sketch, "E85", {"start": v(15, 120) * mm, "mid": v(0, 135) * mm, "end": v(-15, 120) * mm});
            skLineSegment(sketch, "E86", {"start": v(80, 0) * mm, "end": v(-80, 0) * mm, "construction": true});
            skLineSegment(sketch, "E87.MirrorCS", {"start": v(0, -90) * mm, "end": v(0, -120) * mm, "construction": true});
            skCircle(sketch, "E88.MirrorC", {"center": v(0, -120) * mm, "radius": 6 * mm});
            skLineSegment(sketch, "E89.MirrorCS", {"start": v(15, -108) * mm, "end": v(15, -120) * mm});
            skArc(sketch, "E90.MirrorCS", {"start": v(15, -120) * mm, "mid": v(0, -135) * mm, "end": v(-15, -120) * mm});
            skLineSegment(sketch, "E91.MirrorCS", {"start": v(-15, -108) * mm, "end": v(-15, -120) * mm});
            skLineSegment(sketch, "E92.MirrorCS", {"start": v(-33, -90) * mm, "end": v(-15, -108) * mm});
            skLineSegment(sketch, "E93.MirrorCS", {"start": v(33, -90) * mm, "end": v(15, -108) * mm});
            skSolve(sketch);
        }
        {
            var Q0;
            Q0=makeQuery(id+"F16.imprint","IMPRINT",FACE,{"disambiguationData":[TD([[makeQuery(id+"F16.imprint","IMPRINT",EDGE,{"derivedFrom":sQuery(id+"F16.wireOp",EDGE,"E80")}),-1.0]])]});
            var Q1;
            Q1=makeQuery(id+"F16.imprint","IMPRINT",FACE,{"disambiguationData":[TD([[makeQuery(id+"F16.imprint","IMPRINT",EDGE,{"derivedFrom":makeQuery(id+"F1.opExtrude","CAP_EDGE",EDGE,{"disambiguationData":[OSD([sQuery(id+"F0.wireOp",EDGE,"E1.left")])],"isStart":true})}),-1.0]])]});
            var Q2;
            Q2=makeQuery(id+"F16.imprint","IMPRINT",FACE,{"disambiguationData":[TD([[makeQuery(id+"F16.imprint","IMPRINT",EDGE,{"derivedFrom":sQuery(id+"F16.wireOp",EDGE,"E88.MirrorC")}),1.0]])]});
            var Q3;
            Q3=makeQuery(id+"F2.opExtrude","CAP_FACE",FACE,{"disambiguationData":[OSD([sQuery(id+"F0.wireOp",EDGE,"E12"),sQuery(id+"F0.wireOp",EDGE,"E13"),sQuery(id+"F0.wireOp",EDGE,"E14"),sQuery(id+"F0.wireOp",EDGE,"E15"),sQuery(id+"F0.wireOp",EDGE,"E17.filletArc"),sQuery(id+"F0.wireOp",EDGE,"E18.filletArc"),sQuery(id+"F0.wireOp",EDGE,"E19.filletArc"),sQuery(id+"F0.wireOp",EDGE,"E20.filletArc"),sQuery(id+"F0.wireOp",EDGE,"E25.0"),sQuery(id+"F0.wireOp",EDGE,"E25.1"),sQuery(id+"F0.wireOp",EDGE,"E25.2"),sQuery(id+"F0.wireOp",EDGE,"E25.3"),sQuery(id+"F0.wireOp",EDGE,"E25.4"),sQuery(id+"F0.wireOp",EDGE,"E25.5"),sQuery(id+"F0.wireOp",EDGE,"E25.6"),sQuery(id+"F0.wireOp",EDGE,"E25.7")])],"isStart":false});
            extrude(context, id + "F17", {"entities" : qUnion([Q0, Q1, Q2]), "endBound" : BoundingType.UP_TO_SURFACE, "depth" : 25 * mm, "endBoundEntityFace" : qUnion([Q3]), "offsetDistance" : 25 * mm});
        }
    });
